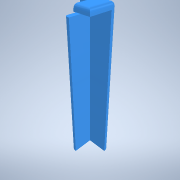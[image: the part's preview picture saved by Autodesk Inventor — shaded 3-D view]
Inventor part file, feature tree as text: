
AUTODESK INVENTOR PART (.ipt)
format: ipt  version: 2021 (Build 250183000, 183)  size: 148,480 bytes
history: native  units: mm
features: extrude x4, sketch x3, fillet x1
ambient origin geometry x8: Origin, YZ Plane, XZ Plane, XY Plane, X Axis, Y Axis, Z Axis, Center Point
bodies: Solid1 (feature_tree)
feature tree (8):
  extrude  "Extrusion1"  Depth=15.0mm
  extrude  "Extrusion3"  Depth=3.0mm
  extrude  "Extrusion4"  Depth=12.0mm
  fillet  "Fillet3"  Radius=3.0mm
  extrude  "Extrusion7"  Depth=3.0mm TaperAngle=0.0deg
  sketch  "Sketch4"  dims[d0=15.0mm d1=15.0mm]
  sketch  "Sketch6"  dims[d2=86.0mm d3=0.0mm d10=3.0mm]
  sketch  "Sketch11"  dims[d11=12.0mm d12=12.0mm d13=3.0mm d14=3.0mm d15=0.0mm d16=12.0mm d17=0.0mm d18=2.0mm d31=6.0mm d32=0.0mm]
